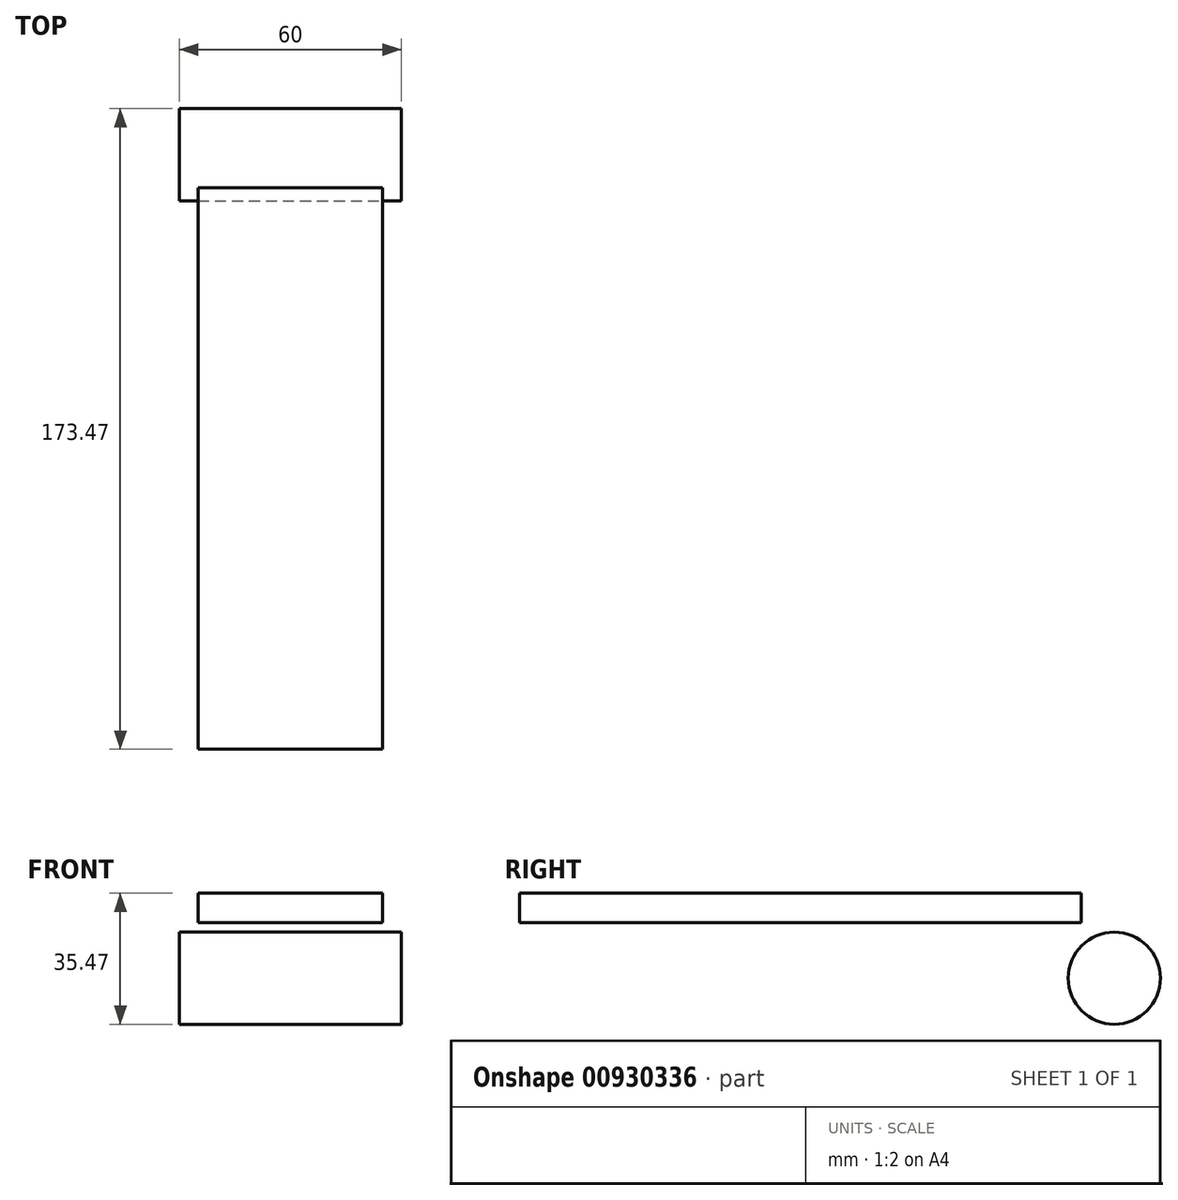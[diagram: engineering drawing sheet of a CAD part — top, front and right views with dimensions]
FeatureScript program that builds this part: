
annotation { "Feature Type Name" : "Feature", "Feature Type Description" : "" }
export const myFeature = defineFeature(function(context is Context, id is Id, definition is map)
    precondition{}
    {
        {
            var Q0;
            Q0=qCreatedBy(makeId("Top.planeOp"),FACE);
            var sketch = newSketch(context, id + "F0", { "sketchPlane" : qUnion([Q0])});
            skLineSegment(sketch, "E0.bottom", {"start": v(30, 100) * mm, "end": v(-30, 100) * mm});
            skLineSegment(sketch, "E0.top", {"start": v(30, -100) * mm, "end": v(-30, -100) * mm});
            skLineSegment(sketch, "E0.left", {"start": v(30, 100) * mm, "end": v(30, -100) * mm});
            skLineSegment(sketch, "E0.right", {"start": v(-30, 100) * mm, "end": v(-30, -100) * mm});
            skPoint(sketch, "E0.middle", {"position": v(0, 0) * mm});
            skSolve(sketch);
        }
        {
            var Q0;
            Q0 = qSketchRegion(id + "F0", true);
            extrude(context, id + "F1", {"entities" : qUnion([Q0]), "depth" : 10 * mm, "offsetDistance" : 25 * mm});
        }
        {
            var Q0;
            Q0=qCreatedBy(makeId("Right.planeOp"),FACE);
            var sketch = newSketch(context, id + "F2", { "sketchPlane" : qUnion([Q0])});
            skLineSegment(sketch, "E1.bottom", {"start": v(-100, 0) * mm, "end": v(-70, 0) * mm});
            skLineSegment(sketch, "E1.top", {"start": v(-100, -20) * mm, "end": v(-70, -20) * mm});
            skLineSegment(sketch, "E1.left", {"start": v(-100, 0) * mm, "end": v(-100, -20) * mm});
            skLineSegment(sketch, "E1.right", {"start": v(-70, 0) * mm, "end": v(-70, -20) * mm});
            skLineSegment(sketch, "E2.MirrorCS", {"start": v(100, -20) * mm, "end": v(70, -20) * mm});
            skLineSegment(sketch, "E3.MirrorCS", {"start": v(70, 0) * mm, "end": v(70, -20) * mm});
            skLineSegment(sketch, "E4.MirrorCS", {"start": v(100, 0) * mm, "end": v(100, -20) * mm});
            skLineSegment(sketch, "E5.MirrorCS", {"start": v(100, 0) * mm, "end": v(70, 0) * mm});
            skSolve(sketch);
        }
        {
            var Q0;
            Q0 = qSketchRegion(id + "F2", true);
            extrude(context, id + "F3", {"entities" : qUnion([Q0]), "operationType" : NewBodyOperationType.ADD, "endBound" : BoundingType.SYMMETRIC, "depth" : 60 * mm, "offsetDistance" : 25 * mm});
        }
        {
            var Q0;
            Q0=makeQuery(id+"F1.opExtrude","CAP_FACE",FACE,{"disambiguationData":[OSD([sQuery(id+"F0.wireOp",EDGE,"E0.bottom"),sQuery(id+"F0.wireOp",EDGE,"E0.top"),sQuery(id+"F0.wireOp",EDGE,"E0.left"),sQuery(id+"F0.wireOp",EDGE,"E0.right")])],"isStart":false});
            var sketch = newSketch(context, id + "F4", { "sketchPlane" : qUnion([Q0])});
            skLineSegment(sketch, "E6.bottom", {"start": v(25, 76) * mm, "end": v(-25, 76) * mm});
            skLineSegment(sketch, "E6.top", {"start": v(25, -76) * mm, "end": v(-25, -76) * mm});
            skLineSegment(sketch, "E6.left", {"start": v(25, 76) * mm, "end": v(25, -76) * mm});
            skLineSegment(sketch, "E6.right", {"start": v(-25, 76) * mm, "end": v(-25, -76) * mm});
            skPoint(sketch, "E6.middle", {"position": v(0, 0) * mm});
            skSolve(sketch);
        }
        {
            var Q0;
            Q0 = qSketchRegion(id + "F4", true);
            extrude(context, id + "F5", {"entities" : qUnion([Q0]), "operationType" : NewBodyOperationType.ADD, "depth" : 8 * mm, "offsetDistance" : 25 * mm});
        }
        {
            var Q0;
            Q0=makeQuery(id+"F3.boolean.opBoolean","MERGE",FACE,{"derivedFrom":[makeQuery(id+"F1.opExtrude","SWEPT_FACE",FACE,{"disambiguationData":[OSD([sQuery(id+"F0.wireOp",EDGE,"E0.left")])]}),makeQuery(id+"F3.opExtrude","CAP_FACE",FACE,{"disambiguationData":[OSD([sQuery(id+"F2.wireOp",EDGE,"E1.bottom"),sQuery(id+"F2.wireOp",EDGE,"E1.top"),sQuery(id+"F2.wireOp",EDGE,"E1.left"),sQuery(id+"F2.wireOp",EDGE,"E1.right")])],"isStart":false}),makeQuery(id+"F3.opExtrude","CAP_FACE",FACE,{"disambiguationData":[OSD([sQuery(id+"F2.wireOp",EDGE,"E2.MirrorCS"),sQuery(id+"F2.wireOp",EDGE,"E3.MirrorCS"),sQuery(id+"F2.wireOp",EDGE,"E4.MirrorCS"),sQuery(id+"F2.wireOp",EDGE,"E5.MirrorCS")])],"isStart":false})]});
            var sketch = newSketch(context, id + "F6", { "sketchPlane" : qUnion([Q0])});
            skCircle(sketch, "E7", {"center": v(-85, -5) * mm, "radius": 12.47 * mm});
            skPoint(sketch, "E7.centerSnap0", {"position": v(-85, -20) * mm});
            skPoint(sketch, "E7.centerSnap1", {"position": v(-100, -5) * mm});
            skCircle(sketch, "E8.MirrorC", {"center": v(85, -5) * mm, "radius": 12.47 * mm});
            skSolve(sketch);
        }
        {
            var Q0;
            Q0=makeQuery(id+"F6.imprint","IMPRINT",FACE,{"disambiguationData":[TD([[makeQuery(id+"F6.imprint","IMPRINT",EDGE,{"derivedFrom":sQuery(id+"F6.wireOp",EDGE,"E7")}),1.0]])]});
            var Q1;
            Q1=makeQuery(id+"F6.imprint","IMPRINT",FACE,{"disambiguationData":[TD([[makeQuery(id+"F6.imprint","IMPRINT",EDGE,{"derivedFrom":sQuery(id+"F6.wireOp",EDGE,"E8.MirrorC")}),-1.0]])]});
            extrude(context, id + "F7", {"entities" : qUnion([Q0, Q1]), "operationType" : NewBodyOperationType.REMOVE, "endBound" : BoundingType.THROUGH_ALL, "oppositeDirection" : true, "depth" : 25 * mm, "offsetDistance" : 25 * mm});
        }
    });
